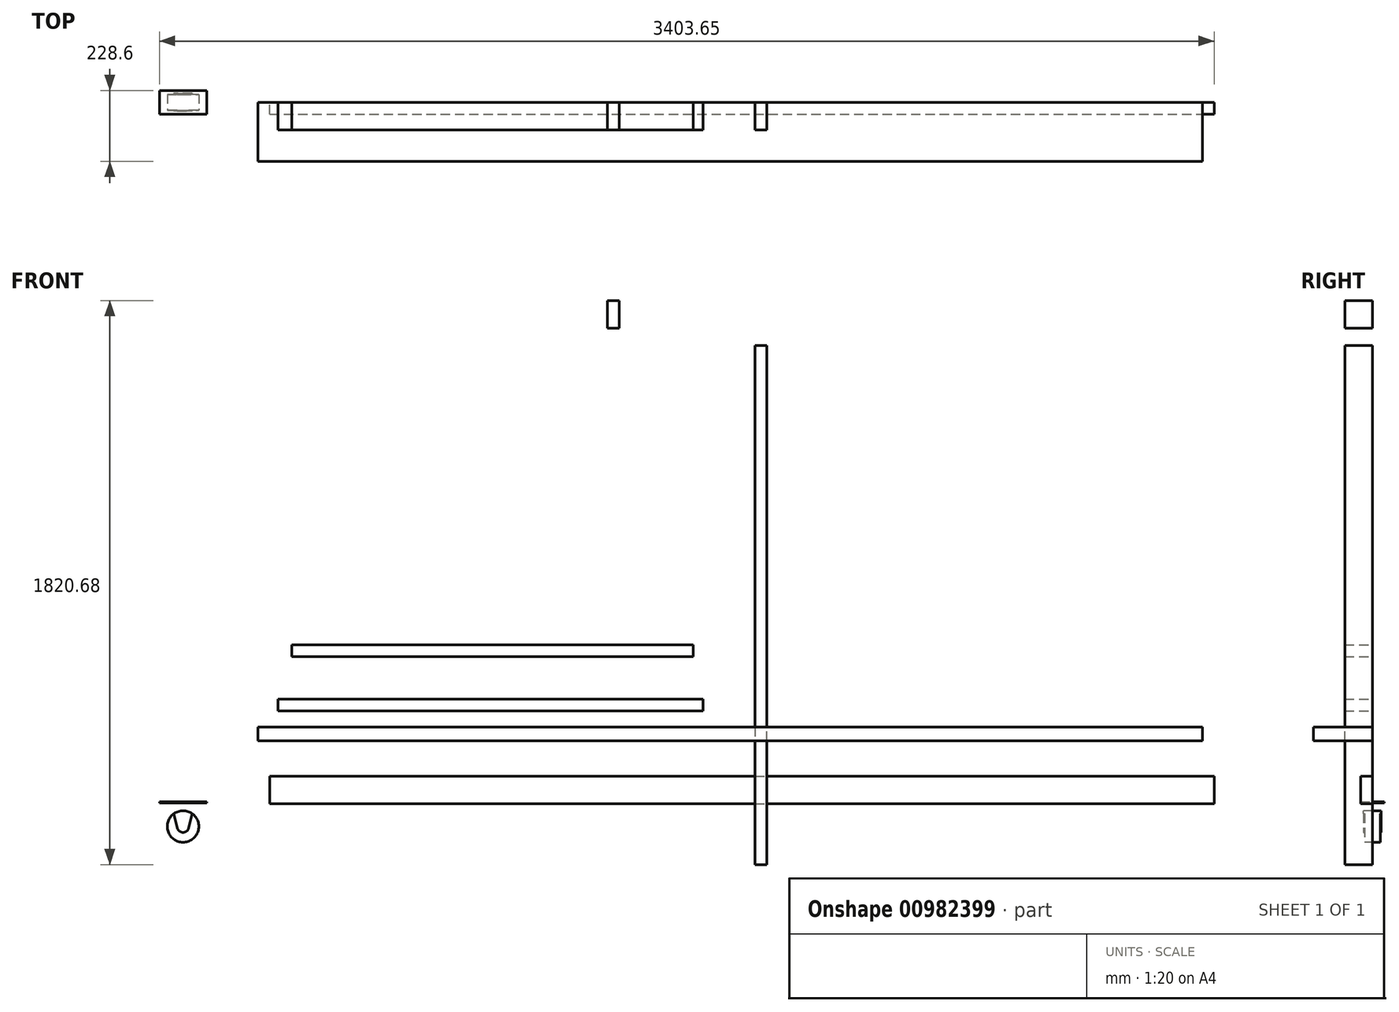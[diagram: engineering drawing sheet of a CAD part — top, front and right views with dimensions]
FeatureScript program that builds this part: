
annotation { "Feature Type Name" : "Feature", "Feature Type Description" : "" }
export const myFeature = defineFeature(function(context is Context, id is Id, definition is map)
    precondition{}
    {
        {
            var Q0;
            Q0=qCreatedBy(makeId("Front.planeOp"),FACE);
            var sketch = newSketch(context, id + "F0", { "sketchPlane" : qUnion([Q0])});
            skLineSegment(sketch, "E0", {"start": v(127.8, 1640.18) * mm, "end": v(89.7, 1640.18) * mm});
            skLineSegment(sketch, "E1", {"start": v(89.7, 1640.18) * mm, "end": v(89.7, -36.22) * mm});
            skLineSegment(sketch, "E2", {"start": v(89.7, -36.22) * mm, "end": v(127.8, -36.22) * mm});
            skLineSegment(sketch, "E3", {"start": v(127.8, -36.22) * mm, "end": v(127.8, 1640.18) * mm});
            skSolve(sketch);
        }
        {
            var Q0;
            Q0=makeQuery(id+"F0.imprint","IMPRINT",FACE,{"disambiguationData":[TD([[makeQuery(id+"F0.imprint","IMPRINT",EDGE,{"derivedFrom":sQuery(id+"F0.wireOp",EDGE,"E0")}),1.0]])]});
            extrude(context, id + "F1", {"entities" : qUnion([Q0]), "depth" : 88.9 * mm, "offsetDistance" : 25.4 * mm});
        }
        {
            var Q0;
            Q0=qCreatedBy(makeId("Front.planeOp"),FACE);
            var sketch = newSketch(context, id + "F2", { "sketchPlane" : qUnion([Q0])});
            skLineSegment(sketch, "E4.bottom", {"start": v(-386.52, 1784.46) * mm, "end": v(-348.42, 1784.46) * mm});
            skLineSegment(sketch, "E4.top", {"start": v(-386.52, 1695.56) * mm, "end": v(-348.42, 1695.56) * mm});
            skLineSegment(sketch, "E4.left", {"start": v(-386.52, 1784.46) * mm, "end": v(-386.52, 1695.56) * mm});
            skLineSegment(sketch, "E4.right", {"start": v(-348.42, 1784.46) * mm, "end": v(-348.42, 1695.56) * mm});
            skSolve(sketch);
        }
        {
            var Q0;
            Q0=qSketchRegion(id+"F2",true);
            extrude(context, id + "F3", {"entities" : qUnion([Q0]), "depth" : 88.9 * mm, "offsetDistance" : 25.4 * mm});
        }
        {
            var Q0;
            Q0=qCreatedBy(makeId("Front.planeOp"),FACE);
            var sketch = newSketch(context, id + "F4", { "sketchPlane" : qUnion([Q0])});
            skLineSegment(sketch, "E5.bottom", {"start": v(-1449.26, 497.5) * mm, "end": v(-77.66, 497.5) * mm});
            skLineSegment(sketch, "E5.top", {"start": v(-1449.26, 459.4) * mm, "end": v(-77.66, 459.4) * mm});
            skLineSegment(sketch, "E5.left", {"start": v(-1449.26, 497.5) * mm, "end": v(-1449.26, 459.4) * mm});
            skLineSegment(sketch, "E5.right", {"start": v(-77.66, 497.5) * mm, "end": v(-77.66, 459.4) * mm});
            skSolve(sketch);
        }
        {
            var Q0;
            Q0=qSketchRegion(id+"F4",true);
            extrude(context, id + "F5", {"entities" : qUnion([Q0]), "depth" : 88.9 * mm, "offsetDistance" : 25.4 * mm});
        }
        {
            var Q0;
            Q0=qCreatedBy(makeId("Front.planeOp"),FACE);
            var sketch = newSketch(context, id + "F6", { "sketchPlane" : qUnion([Q0])});
            skLineSegment(sketch, "E6.bottom", {"start": v(-1832.15, 166.2) * mm, "end": v(-1679.75, 166.2) * mm});
            skLineSegment(sketch, "E6.top", {"start": v(-1832.15, 163.03) * mm, "end": v(-1679.75, 163.03) * mm});
            skLineSegment(sketch, "E6.left", {"start": v(-1832.15, 166.2) * mm, "end": v(-1832.15, 163.03) * mm});
            skLineSegment(sketch, "E6.right", {"start": v(-1679.75, 166.2) * mm, "end": v(-1679.75, 163.03) * mm});
            skCircle(sketch, "E7", {"center": v(-1755.95, 86.83) * mm, "radius": 50.8 * mm});
            skLineSegment(sketch, "E8", {"start": v(-1755.95, 86.83) * mm, "end": v(-1755.95, 163.03) * mm, "construction": true});
            skLineSegment(sketch, "E9", {"start": v(-1774.46, 82.34) * mm, "end": v(-1794.05, 163.03) * mm});
            skLineSegment(sketch, "E10", {"start": v(-1794.05, 163.03) * mm, "end": v(-1717.85, 163.03) * mm});
            skLineSegment(sketch, "E11", {"start": v(-1717.85, 163.03) * mm, "end": v(-1737.44, 82.34) * mm});
            skArc(sketch, "E12", {"start": v(-1774.46, 82.34) * mm, "mid": v(-1755.95, 67.78) * mm, "end": v(-1737.44, 82.34) * mm});
            skSolve(sketch);
        }
        {
            var Q0;
            Q0=makeQuery(id+"F6.imprint","IMPRINT",FACE,{"disambiguationData":[TD([[makeQuery(id+"F6.imprint","IMPRINT",EDGE,{"derivedFrom":sQuery(id+"F6.wireOp",EDGE,"E6.bottom")}),-1.0]])]});
            extrude(context, id + "F7", {"entities" : qUnion([Q0]), "endBound" : BoundingType.SYMMETRIC, "depth" : 76.2 * mm, "offsetDistance" : 25.4 * mm});
        }
        {
            var Q0;
            {var subQ5=sQuery(id+"F6.wireOp",EDGE,"E12");Q0=makeQuery(id+"F6.imprint","IMPRINT",FACE,{"disambiguationData":[TD([[makeQuery(id+"F6.imprint","IMPRINT",EDGE,{"derivedFrom":subQ5}),1.0]])]});}
            var Q1;
            {var subQ5=sQuery(id+"F6.wireOp",EDGE,"E10");Q1=makeQuery(id+"F6.imprint","IMPRINT",FACE,{"disambiguationData":[TD([[makeQuery(id+"F6.imprint","IMPRINT",EDGE,{"derivedFrom":subQ5}),-1.0]])]});}
            extrude(context, id + "F8", {"entities" : qUnion([Q0, Q1]), "operationType" : NewBodyOperationType.ADD, "depth" : -28.57 * mm, "offsetDistance" : 25.4 * mm, "hasSecondDirection" : true, "secondDirectionOppositeDirection" : true, "secondDirectionDepth" : 25.4 * mm});
        }
        {
            var Q0;
            {var subQ5=sQuery(id+"F6.wireOp",EDGE,"E10");Q0=makeQuery(id+"F6.imprint","IMPRINT",FACE,{"disambiguationData":[TD([[makeQuery(id+"F6.imprint","IMPRINT",EDGE,{"derivedFrom":subQ5}),-1.0]])]});}
            var Q1;
            {var subQ5=sQuery(id+"F6.wireOp",EDGE,"E12");Q1=makeQuery(id+"F6.imprint","IMPRINT",FACE,{"disambiguationData":[TD([[makeQuery(id+"F6.imprint","IMPRINT",EDGE,{"derivedFrom":subQ5}),1.0]])]});}
            extrude(context, id + "F9", {"entities" : qUnion([Q0, Q1]), "operationType" : NewBodyOperationType.ADD, "depth" : 28.57 * mm, "offsetDistance" : 25.4 * mm, "hasSecondDirection" : true, "secondDirectionOppositeDirection" : true, "secondDirectionDepth" : -25.4 * mm});
        }
        {
            var Q0;
            Q0=makeQuery(id+"F6.imprint","IMPRINT",FACE,{"disambiguationData":[TD([[makeQuery(id+"F6.imprint","IMPRINT",EDGE,{"derivedFrom":sQuery(id+"F6.wireOp",EDGE,"E7")}),1.0]])]});
            extrude(context, id + "F10", {"entities" : qUnion([Q0]), "operationType" : NewBodyOperationType.ADD, "endBound" : BoundingType.SYMMETRIC, "depth" : 50.8 * mm, "offsetDistance" : 25.4 * mm});
        }
        {
            var Q0;
            Q0=qCreatedBy(makeId("Front.planeOp"),FACE);
            var sketch = newSketch(context, id + "F11", { "sketchPlane" : qUnion([Q0])});
            skLineSegment(sketch, "E13.bottom", {"start": v(-1405.01, 673.22) * mm, "end": v(-109.61, 673.22) * mm});
            skLineSegment(sketch, "E13.top", {"start": v(-1405.01, 635.12) * mm, "end": v(-109.61, 635.12) * mm});
            skLineSegment(sketch, "E13.left", {"start": v(-1405.01, 673.22) * mm, "end": v(-1405.01, 635.12) * mm});
            skLineSegment(sketch, "E13.right", {"start": v(-109.61, 673.22) * mm, "end": v(-109.61, 635.12) * mm});
            skSolve(sketch);
        }
        {
            var Q0;
            Q0=makeQuery(id+"F11.imprint","IMPRINT",FACE,{"disambiguationData":[TD([[makeQuery(id+"F11.imprint","IMPRINT",EDGE,{"derivedFrom":sQuery(id+"F11.wireOp",EDGE,"E13.bottom")}),-1.0]])]});
            extrude(context, id + "F12", {"entities" : qUnion([Q0]), "depth" : 88.9 * mm, "offsetDistance" : 25.4 * mm});
        }
        {
            var Q0;
            Q0=qCreatedBy(makeId("Front.planeOp"),FACE);
            var sketch = newSketch(context, id + "F13", { "sketchPlane" : qUnion([Q0])});
            skLineSegment(sketch, "E14.bottom", {"start": v(-1514.83, 407.8) * mm, "end": v(1533.17, 407.8) * mm});
            skLineSegment(sketch, "E14.top", {"start": v(-1514.83, 363.36) * mm, "end": v(1533.17, 363.36) * mm});
            skLineSegment(sketch, "E14.left", {"start": v(-1514.83, 407.8) * mm, "end": v(-1514.83, 363.36) * mm});
            skLineSegment(sketch, "E14.right", {"start": v(1533.17, 407.8) * mm, "end": v(1533.17, 363.36) * mm});
            skSolve(sketch);
        }
        {
            var Q0;
            Q0=makeQuery(id+"F13.imprint","IMPRINT",FACE,{"disambiguationData":[TD([[makeQuery(id+"F13.imprint","IMPRINT",EDGE,{"derivedFrom":sQuery(id+"F13.wireOp",EDGE,"E14.bottom")}),-1.0]])]});
            extrude(context, id + "F14", {"entities" : qUnion([Q0]), "depth" : 190.5 * mm, "offsetDistance" : 25.4 * mm});
        }
        {
            var Q0;
            Q0=qCreatedBy(makeId("Front.planeOp"),FACE);
            var sketch = newSketch(context, id + "F15", { "sketchPlane" : qUnion([Q0])});
            skLineSegment(sketch, "E15.bottom", {"start": v(-1476.5, 248.64) * mm, "end": v(1571.5, 248.64) * mm});
            skLineSegment(sketch, "E15.top", {"start": v(-1476.5, 159.74) * mm, "end": v(1571.5, 159.74) * mm});
            skLineSegment(sketch, "E15.left", {"start": v(-1476.5, 248.64) * mm, "end": v(-1476.5, 159.74) * mm});
            skLineSegment(sketch, "E15.right", {"start": v(1571.5, 248.64) * mm, "end": v(1571.5, 159.74) * mm});
            skSolve(sketch);
        }
        {
            var Q0;
            Q0=makeQuery(id+"F15.imprint","IMPRINT",FACE,{"disambiguationData":[TD([[makeQuery(id+"F15.imprint","IMPRINT",EDGE,{"derivedFrom":sQuery(id+"F15.wireOp",EDGE,"E15.bottom")}),-1.0]])]});
            extrude(context, id + "F16", {"entities" : qUnion([Q0]), "depth" : 38.1 * mm, "offsetDistance" : 25.4 * mm});
        }
    });
